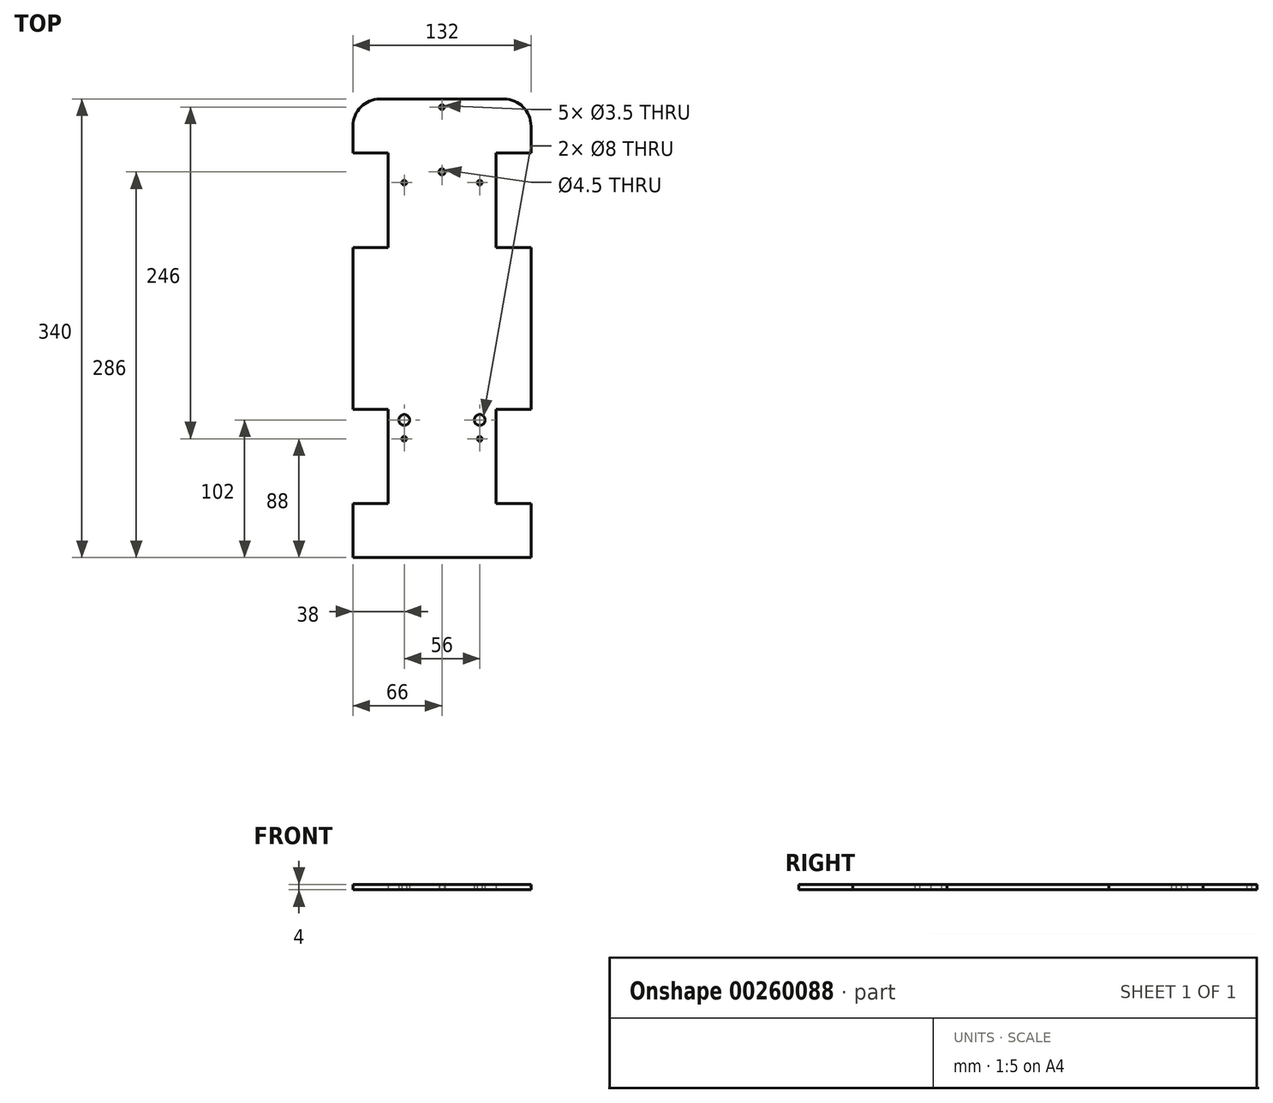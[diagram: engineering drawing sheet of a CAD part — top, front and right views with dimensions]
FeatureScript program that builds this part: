
annotation { "Feature Type Name" : "Feature", "Feature Type Description" : "" }
export const myFeature = defineFeature(function(context is Context, id is Id, definition is map)
    precondition{}
    {
        {
            var Q0;
            Q0=qCreatedBy(makeId("Top.planeOp"),FACE);
            var sketch = newSketch(context, id + "F0", { "sketchPlane" : qUnion([Q0])});
            skLineSegment(sketch, "E0.bottom", {"start": v(-66, 90) * mm, "end": v(0, 90) * mm});
            skLineSegment(sketch, "E0.top", {"start": v(-66, -230) * mm, "end": v(0, -230) * mm});
            skLineSegment(sketch, "E0.left", {"start": v(-66, 90) * mm, "end": v(-66, 70) * mm});
            skLineSegment(sketch, "E0.right", {"start": v(0, 90) * mm, "end": v(0, -230) * mm});
            skLineSegment(sketch, "E1.bottom", {"start": v(-66, 70) * mm, "end": v(-40, 70) * mm});
            skLineSegment(sketch, "E1.top", {"start": v(-66, 0) * mm, "end": v(-40, 0) * mm});
            skLineSegment(sketch, "E1.right", {"start": v(-40, 70) * mm, "end": v(-40, 0) * mm});
            skLineSegment(sketch, "E2.bottom", {"start": v(-66, -120) * mm, "end": v(-40, -120) * mm});
            skLineSegment(sketch, "E2.top", {"start": v(-66, -190) * mm, "end": v(-40, -190) * mm});
            skLineSegment(sketch, "E2.right", {"start": v(-40, -120) * mm, "end": v(-40, -190) * mm});
            skLineSegment(sketch, "E3.trimOffspring", {"start": v(-66, -190) * mm, "end": v(-66, -230) * mm});
            skLineSegment(sketch, "E4.trimOffspring", {"start": v(-66, 0) * mm, "end": v(-66, -120) * mm});
            skLineSegment(sketch, "E5.bottom", {"start": v(-46, 110) * mm, "end": v(-40, 110) * mm});
            skLineSegment(sketch, "E5.top", {"start": v(-66, 90) * mm, "end": v(-40, 90) * mm});
            skLineSegment(sketch, "E5.left", {"start": v(-66, 90) * mm, "end": v(-66, 90) * mm});
            skLineSegment(sketch, "E5.right", {"start": v(-40, 110) * mm, "end": v(-40, 90) * mm});
            skPoint(sketch, "E6.visualSharp", {"position": v(-66, 110) * mm});
            skArc(sketch, "E6.filletArc", {"start": v(-46, 110) * mm, "mid": v(-60.14, 104.14) * mm, "end": v(-66, 90) * mm});
            skLineSegment(sketch, "E7.bottom", {"start": v(-40, 110) * mm, "end": v(0, 110) * mm});
            skLineSegment(sketch, "E7.top", {"start": v(-40, 90) * mm, "end": v(0, 90) * mm});
            skLineSegment(sketch, "E7.right", {"start": v(0, 110) * mm, "end": v(0, 90) * mm});
            skLineSegment(sketch, "E8.MirrorCS", {"start": v(40, 110) * mm, "end": v(0, 110) * mm});
            skArc(sketch, "E9.MirrorCS", {"start": v(46, 110) * mm, "mid": v(60.14, 104.14) * mm, "end": v(66, 90) * mm});
            skLineSegment(sketch, "E10.MirrorCS", {"start": v(46, 110) * mm, "end": v(40, 110) * mm});
            skLineSegment(sketch, "E11.MirrorCS", {"start": v(66, 90) * mm, "end": v(0, 90) * mm});
            skLineSegment(sketch, "E12.MirrorCS", {"start": v(66, 90) * mm, "end": v(66, 70) * mm});
            skLineSegment(sketch, "E13.MirrorCS", {"start": v(66, 70) * mm, "end": v(40, 70) * mm});
            skLineSegment(sketch, "E14.MirrorCS", {"start": v(66, 0) * mm, "end": v(40, 0) * mm});
            skLineSegment(sketch, "E15.MirrorCS", {"start": v(40, 70) * mm, "end": v(40, 0) * mm});
            skLineSegment(sketch, "E16.MirrorCS", {"start": v(66, 0) * mm, "end": v(66, -120) * mm});
            skLineSegment(sketch, "E17.MirrorCS", {"start": v(40, -120) * mm, "end": v(40, -190) * mm});
            skLineSegment(sketch, "E18.MirrorCS", {"start": v(66, -120) * mm, "end": v(40, -120) * mm});
            skLineSegment(sketch, "E19.MirrorCS", {"start": v(66, -190) * mm, "end": v(40, -190) * mm});
            skLineSegment(sketch, "E20.MirrorCS", {"start": v(66, -190) * mm, "end": v(66, -230) * mm});
            skLineSegment(sketch, "E21.MirrorCS", {"start": v(66, -230) * mm, "end": v(0, -230) * mm});
            skLineSegment(sketch, "E22.left", {"start": v(-40, -120) * mm, "end": v(-40, -142) * mm});
            skLineSegment(sketch, "E23.right", {"start": v(-40, -142) * mm, "end": v(-40, -142) * mm});
            skLineSegment(sketch, "E24.MirrorCS", {"start": v(40, -142) * mm, "end": v(16, -142) * mm});
            skLineSegment(sketch, "E25.MirrorCS", {"start": v(28, -142) * mm, "end": v(40, -142) * mm});
            skLineSegment(sketch, "E26.top", {"start": v(-40, -128) * mm, "end": v(-28, -128) * mm});
            skLineSegment(sketch, "E26.left", {"start": v(-40, -120) * mm, "end": v(-40, -128) * mm});
            skLineSegment(sketch, "E26.right", {"start": v(-28, -120) * mm, "end": v(-28, -128) * mm});
            skLineSegment(sketch, "E27.MirrorCS", {"start": v(28, -120) * mm, "end": v(28, -128) * mm});
            skLineSegment(sketch, "E28.MirrorCS", {"start": v(40, -128) * mm, "end": v(28, -128) * mm});
            skLineSegment(sketch, "E29.bottom", {"start": v(-40, -142) * mm, "end": v(-28, -142) * mm});
            skLineSegment(sketch, "E29.left", {"start": v(-40, -142) * mm, "end": v(-40, -135.6) * mm});
            skLineSegment(sketch, "E29.right", {"start": v(-28, -142) * mm, "end": v(-28, -135.6) * mm});
            skLineSegment(sketch, "E30.top", {"start": v(-40, 48) * mm, "end": v(-28, 48) * mm});
            skLineSegment(sketch, "E30.left", {"start": v(-40, 70) * mm, "end": v(-40, 48) * mm});
            skLineSegment(sketch, "E30.right", {"start": v(-28, 52.96) * mm, "end": v(-28, 48) * mm});
            skLineSegment(sketch, "E31.bottom", {"start": v(-41.22, 70) * mm, "end": v(-40, 70) * mm});
            skLineSegment(sketch, "E32.MirrorCS", {"start": v(28, 52.96) * mm, "end": v(28, 48) * mm});
            skLineSegment(sketch, "E33.MirrorCS", {"start": v(40, 48) * mm, "end": v(28, 48) * mm});
            skLineSegment(sketch, "E34.left", {"start": v(-40, 62.87) * mm, "end": v(-40, 56) * mm});
            skLineSegment(sketch, "E34.right", {"start": v(0, 62.87) * mm, "end": v(0, 56) * mm});
            skLineSegment(sketch, "E35.bottom", {"start": v(-6.64, 110) * mm, "end": v(0, 110) * mm});
            skLineSegment(sketch, "E35.right", {"start": v(0, 110) * mm, "end": v(0, 104) * mm});
            skSolve(sketch);
        }
        {
            var Q0;
            Q0=makeQuery(id+"F0.imprint","IMPRINT",FACE,{"disambiguationData":[TD([[makeQuery(id+"F0.imprint","IMPRINT",EDGE,{"derivedFrom":sQuery(id+"F0.wireOp",EDGE,"E0.top")}),1.0]])]});
            var Q1;
            Q1=makeQuery(id+"F0.imprint","IMPRINT",FACE,{"disambiguationData":[TD([[makeQuery(id+"F0.imprint","IMPRINT",EDGE,{"derivedFrom":sQuery(id+"F0.wireOp",EDGE,"E0.right")}),1.0]])]});
            var Q2;
            Q2=makeQuery(id+"F0.imprint","IMPRINT",FACE,{"disambiguationData":[TD([[makeQuery(id+"F0.imprint","IMPRINT",EDGE,{"derivedFrom":sQuery(id+"F0.wireOp",EDGE,"E7.right")}),1.0]])]});
            var Q3;
            Q3=makeQuery(id+"F0.imprint","IMPRINT",FACE,{"disambiguationData":[TD([[makeQuery(id+"F0.imprint","IMPRINT",EDGE,{"derivedFrom":sQuery(id+"F0.wireOp",EDGE,"E7.bottom")}),-1.0]])]});
            var Q4;
            Q4=makeQuery(id+"F0.imprint","IMPRINT",FACE,{"disambiguationData":[TD([[makeQuery(id+"F0.imprint","IMPRINT",EDGE,{"derivedFrom":sQuery(id+"F0.wireOp",EDGE,"E5.bottom")}),-1.0]])]});
            extrude(context, id + "F1", {"entities" : qUnion([Q0, Q1, Q2, Q3, Q4]), "depth" : 4 * mm});
        }
        {
            var Q0;
            Q0=sQuery(id+"F0.wireOp",VERTEX,"E26.right.end");
            var Q1;
            Q1=makeQuery(id+"F1.opExtrude","SWEPT_BODY",BODY,{"disambiguationData":[OSD([sQuery(id+"F0.wireOp",EDGE,"E0.top"),sQuery(id+"F0.wireOp",EDGE,"E0.left"),sQuery(id+"F0.wireOp",EDGE,"E1.bottom"),sQuery(id+"F0.wireOp",EDGE,"E1.top"),sQuery(id+"F0.wireOp",EDGE,"E1.right"),sQuery(id+"F0.wireOp",EDGE,"E2.bottom"),sQuery(id+"F0.wireOp",EDGE,"E2.top"),sQuery(id+"F0.wireOp",EDGE,"E2.right"),sQuery(id+"F0.wireOp",EDGE,"E3.trimOffspring"),sQuery(id+"F0.wireOp",EDGE,"E4.trimOffspring"),sQuery(id+"F0.wireOp",EDGE,"E5.bottom"),sQuery(id+"F0.wireOp",EDGE,"E6.filletArc"),sQuery(id+"F0.wireOp",EDGE,"E7.bottom"),sQuery(id+"F0.wireOp",EDGE,"E8.MirrorCS"),sQuery(id+"F0.wireOp",EDGE,"E9.MirrorCS"),sQuery(id+"F0.wireOp",EDGE,"E10.MirrorCS"),sQuery(id+"F0.wireOp",EDGE,"E12.MirrorCS"),sQuery(id+"F0.wireOp",EDGE,"E13.MirrorCS"),sQuery(id+"F0.wireOp",EDGE,"E14.MirrorCS"),sQuery(id+"F0.wireOp",EDGE,"E15.MirrorCS"),sQuery(id+"F0.wireOp",EDGE,"E16.MirrorCS"),sQuery(id+"F0.wireOp",EDGE,"E17.MirrorCS"),sQuery(id+"F0.wireOp",EDGE,"E18.MirrorCS"),sQuery(id+"F0.wireOp",EDGE,"E19.MirrorCS"),sQuery(id+"F0.wireOp",EDGE,"E20.MirrorCS"),sQuery(id+"F0.wireOp",EDGE,"E21.MirrorCS"),sQuery(id+"F0.wireOp",EDGE,"E22.left"),sQuery(id+"F0.wireOp",EDGE,"E26.left")])]});
            hole(context, id + "F2", {"style" : HoleStyle.SIMPLE, "endStyle" : HoleEndStyle.THROUGH, "oppositeDirection" : true, "holeDiameter" : 8 * mm, "tappedDepth" : 12 * mm, "tapClearance" : 3, "locations" : qUnion([Q0]), "scope" : qUnion([Q1])});
        }
        {
            var Q0;
            Q0=sQuery(id+"F0.wireOp",VERTEX,"E29.bottom.end");
            var Q1;
            Q1=sQuery(id+"F0.wireOp",VERTEX,"E25.MirrorCS.start");
            var Q2;
            Q2=makeQuery(id+"F1.opExtrude","SWEPT_BODY",BODY,{"disambiguationData":[OSD([sQuery(id+"F0.wireOp",EDGE,"E0.top"),sQuery(id+"F0.wireOp",EDGE,"E0.left"),sQuery(id+"F0.wireOp",EDGE,"E1.bottom"),sQuery(id+"F0.wireOp",EDGE,"E1.top"),sQuery(id+"F0.wireOp",EDGE,"E1.right"),sQuery(id+"F0.wireOp",EDGE,"E2.bottom"),sQuery(id+"F0.wireOp",EDGE,"E2.top"),sQuery(id+"F0.wireOp",EDGE,"E2.right"),sQuery(id+"F0.wireOp",EDGE,"E3.trimOffspring"),sQuery(id+"F0.wireOp",EDGE,"E4.trimOffspring"),sQuery(id+"F0.wireOp",EDGE,"E5.bottom"),sQuery(id+"F0.wireOp",EDGE,"E6.filletArc"),sQuery(id+"F0.wireOp",EDGE,"E7.bottom"),sQuery(id+"F0.wireOp",EDGE,"E8.MirrorCS"),sQuery(id+"F0.wireOp",EDGE,"E9.MirrorCS"),sQuery(id+"F0.wireOp",EDGE,"E10.MirrorCS"),sQuery(id+"F0.wireOp",EDGE,"E12.MirrorCS"),sQuery(id+"F0.wireOp",EDGE,"E13.MirrorCS"),sQuery(id+"F0.wireOp",EDGE,"E14.MirrorCS"),sQuery(id+"F0.wireOp",EDGE,"E15.MirrorCS"),sQuery(id+"F0.wireOp",EDGE,"E16.MirrorCS"),sQuery(id+"F0.wireOp",EDGE,"E17.MirrorCS"),sQuery(id+"F0.wireOp",EDGE,"E18.MirrorCS"),sQuery(id+"F0.wireOp",EDGE,"E19.MirrorCS"),sQuery(id+"F0.wireOp",EDGE,"E20.MirrorCS"),sQuery(id+"F0.wireOp",EDGE,"E21.MirrorCS"),sQuery(id+"F0.wireOp",EDGE,"E22.left"),sQuery(id+"F0.wireOp",EDGE,"E26.left"),sQuery(id+"F0.wireOp",EDGE,"E29.left")])]});
            hole(context, id + "F3", {"style" : HoleStyle.SIMPLE, "endStyle" : HoleEndStyle.THROUGH, "oppositeDirection" : true, "holeDiameter" : 3.5 * mm, "tappedDepth" : 12 * mm, "tapClearance" : 3, "locations" : qUnion([Q0, Q1]), "scope" : qUnion([Q2])});
        }
        {
            var Q0;
            Q0=sQuery(id+"F0.wireOp",VERTEX,"E28.MirrorCS.end");
            var Q1;
            Q1=makeQuery(id+"F1.opExtrude","SWEPT_BODY",BODY,{"disambiguationData":[OSD([sQuery(id+"F0.wireOp",EDGE,"E0.top"),sQuery(id+"F0.wireOp",EDGE,"E0.left"),sQuery(id+"F0.wireOp",EDGE,"E1.bottom"),sQuery(id+"F0.wireOp",EDGE,"E1.top"),sQuery(id+"F0.wireOp",EDGE,"E1.right"),sQuery(id+"F0.wireOp",EDGE,"E2.bottom"),sQuery(id+"F0.wireOp",EDGE,"E2.top"),sQuery(id+"F0.wireOp",EDGE,"E2.right"),sQuery(id+"F0.wireOp",EDGE,"E3.trimOffspring"),sQuery(id+"F0.wireOp",EDGE,"E4.trimOffspring"),sQuery(id+"F0.wireOp",EDGE,"E5.bottom"),sQuery(id+"F0.wireOp",EDGE,"E6.filletArc"),sQuery(id+"F0.wireOp",EDGE,"E7.bottom"),sQuery(id+"F0.wireOp",EDGE,"E8.MirrorCS"),sQuery(id+"F0.wireOp",EDGE,"E9.MirrorCS"),sQuery(id+"F0.wireOp",EDGE,"E10.MirrorCS"),sQuery(id+"F0.wireOp",EDGE,"E12.MirrorCS"),sQuery(id+"F0.wireOp",EDGE,"E13.MirrorCS"),sQuery(id+"F0.wireOp",EDGE,"E14.MirrorCS"),sQuery(id+"F0.wireOp",EDGE,"E15.MirrorCS"),sQuery(id+"F0.wireOp",EDGE,"E16.MirrorCS"),sQuery(id+"F0.wireOp",EDGE,"E17.MirrorCS"),sQuery(id+"F0.wireOp",EDGE,"E18.MirrorCS"),sQuery(id+"F0.wireOp",EDGE,"E19.MirrorCS"),sQuery(id+"F0.wireOp",EDGE,"E20.MirrorCS"),sQuery(id+"F0.wireOp",EDGE,"E21.MirrorCS"),sQuery(id+"F0.wireOp",EDGE,"E22.left"),sQuery(id+"F0.wireOp",EDGE,"E26.left"),sQuery(id+"F0.wireOp",EDGE,"E29.left")])]});
            hole(context, id + "F4", {"style" : HoleStyle.SIMPLE, "endStyle" : HoleEndStyle.THROUGH, "oppositeDirection" : true, "holeDiameter" : 8 * mm, "tappedDepth" : 12 * mm, "tapClearance" : 3, "locations" : qUnion([Q0]), "scope" : qUnion([Q1])});
        }
        {
            var Q0;
            Q0=sQuery(id+"F0.wireOp",VERTEX,"E30.right.end");
            var Q1;
            Q1=sQuery(id+"F0.wireOp",VERTEX,"E32.MirrorCS.end");
            var Q2;
            Q2=makeQuery(id+"F1.opExtrude","SWEPT_BODY",BODY,{"disambiguationData":[OSD([sQuery(id+"F0.wireOp",EDGE,"E0.top"),sQuery(id+"F0.wireOp",EDGE,"E0.left"),sQuery(id+"F0.wireOp",EDGE,"E1.bottom"),sQuery(id+"F0.wireOp",EDGE,"E1.top"),sQuery(id+"F0.wireOp",EDGE,"E1.right"),sQuery(id+"F0.wireOp",EDGE,"E2.bottom"),sQuery(id+"F0.wireOp",EDGE,"E2.top"),sQuery(id+"F0.wireOp",EDGE,"E2.right"),sQuery(id+"F0.wireOp",EDGE,"E3.trimOffspring"),sQuery(id+"F0.wireOp",EDGE,"E4.trimOffspring"),sQuery(id+"F0.wireOp",EDGE,"E5.bottom"),sQuery(id+"F0.wireOp",EDGE,"E6.filletArc"),sQuery(id+"F0.wireOp",EDGE,"E7.bottom"),sQuery(id+"F0.wireOp",EDGE,"E8.MirrorCS"),sQuery(id+"F0.wireOp",EDGE,"E9.MirrorCS"),sQuery(id+"F0.wireOp",EDGE,"E10.MirrorCS"),sQuery(id+"F0.wireOp",EDGE,"E12.MirrorCS"),sQuery(id+"F0.wireOp",EDGE,"E13.MirrorCS"),sQuery(id+"F0.wireOp",EDGE,"E14.MirrorCS"),sQuery(id+"F0.wireOp",EDGE,"E15.MirrorCS"),sQuery(id+"F0.wireOp",EDGE,"E16.MirrorCS"),sQuery(id+"F0.wireOp",EDGE,"E17.MirrorCS"),sQuery(id+"F0.wireOp",EDGE,"E18.MirrorCS"),sQuery(id+"F0.wireOp",EDGE,"E19.MirrorCS"),sQuery(id+"F0.wireOp",EDGE,"E20.MirrorCS"),sQuery(id+"F0.wireOp",EDGE,"E21.MirrorCS"),sQuery(id+"F0.wireOp",EDGE,"E22.left"),sQuery(id+"F0.wireOp",EDGE,"E26.left"),sQuery(id+"F0.wireOp",EDGE,"E29.left"),sQuery(id+"F0.wireOp",EDGE,"E30.left"),sQuery(id+"F0.wireOp",EDGE,"E31.bottom")])]});
            hole(context, id + "F5", {"style" : HoleStyle.SIMPLE, "endStyle" : HoleEndStyle.THROUGH, "oppositeDirection" : true, "holeDiameter" : 3.5 * mm, "tappedDepth" : 12 * mm, "tapClearance" : 3, "locations" : qUnion([Q0, Q1]), "scope" : qUnion([Q2])});
        }
        {
            var Q0;
            Q0=sQuery(id+"F0.wireOp",VERTEX,"E34.right.end");
            var Q1;
            Q1=makeQuery(id+"F1.opExtrude","SWEPT_BODY",BODY,{"disambiguationData":[OSD([sQuery(id+"F0.wireOp",EDGE,"E0.top"),sQuery(id+"F0.wireOp",EDGE,"E0.left"),sQuery(id+"F0.wireOp",EDGE,"E1.bottom"),sQuery(id+"F0.wireOp",EDGE,"E1.top"),sQuery(id+"F0.wireOp",EDGE,"E1.right"),sQuery(id+"F0.wireOp",EDGE,"E2.bottom"),sQuery(id+"F0.wireOp",EDGE,"E2.top"),sQuery(id+"F0.wireOp",EDGE,"E2.right"),sQuery(id+"F0.wireOp",EDGE,"E3.trimOffspring"),sQuery(id+"F0.wireOp",EDGE,"E4.trimOffspring"),sQuery(id+"F0.wireOp",EDGE,"E5.bottom"),sQuery(id+"F0.wireOp",EDGE,"E6.filletArc"),sQuery(id+"F0.wireOp",EDGE,"E7.bottom"),sQuery(id+"F0.wireOp",EDGE,"E8.MirrorCS"),sQuery(id+"F0.wireOp",EDGE,"E9.MirrorCS"),sQuery(id+"F0.wireOp",EDGE,"E10.MirrorCS"),sQuery(id+"F0.wireOp",EDGE,"E12.MirrorCS"),sQuery(id+"F0.wireOp",EDGE,"E13.MirrorCS"),sQuery(id+"F0.wireOp",EDGE,"E14.MirrorCS"),sQuery(id+"F0.wireOp",EDGE,"E15.MirrorCS"),sQuery(id+"F0.wireOp",EDGE,"E16.MirrorCS"),sQuery(id+"F0.wireOp",EDGE,"E17.MirrorCS"),sQuery(id+"F0.wireOp",EDGE,"E18.MirrorCS"),sQuery(id+"F0.wireOp",EDGE,"E19.MirrorCS"),sQuery(id+"F0.wireOp",EDGE,"E20.MirrorCS"),sQuery(id+"F0.wireOp",EDGE,"E21.MirrorCS"),sQuery(id+"F0.wireOp",EDGE,"E22.left"),sQuery(id+"F0.wireOp",EDGE,"E26.left"),sQuery(id+"F0.wireOp",EDGE,"E29.left"),sQuery(id+"F0.wireOp",EDGE,"E30.left"),sQuery(id+"F0.wireOp",EDGE,"E31.bottom"),sQuery(id+"F0.wireOp",EDGE,"E34.left")])]});
            hole(context, id + "F6", {"style" : HoleStyle.SIMPLE, "endStyle" : HoleEndStyle.THROUGH, "oppositeDirection" : true, "holeDiameter" : 4.5 * mm, "tappedDepth" : 12 * mm, "tapClearance" : 3, "locations" : qUnion([Q0]), "scope" : qUnion([Q1])});
        }
        {
            var Q0;
            Q0=sQuery(id+"F0.wireOp",VERTEX,"E35.right.end");
            var Q1;
            Q1=makeQuery(id+"F1.opExtrude","SWEPT_BODY",BODY,{"disambiguationData":[OSD([sQuery(id+"F0.wireOp",EDGE,"E0.top"),sQuery(id+"F0.wireOp",EDGE,"E0.left"),sQuery(id+"F0.wireOp",EDGE,"E1.bottom"),sQuery(id+"F0.wireOp",EDGE,"E1.top"),sQuery(id+"F0.wireOp",EDGE,"E1.right"),sQuery(id+"F0.wireOp",EDGE,"E2.bottom"),sQuery(id+"F0.wireOp",EDGE,"E2.top"),sQuery(id+"F0.wireOp",EDGE,"E2.right"),sQuery(id+"F0.wireOp",EDGE,"E3.trimOffspring"),sQuery(id+"F0.wireOp",EDGE,"E4.trimOffspring"),sQuery(id+"F0.wireOp",EDGE,"E5.bottom"),sQuery(id+"F0.wireOp",EDGE,"E6.filletArc"),sQuery(id+"F0.wireOp",EDGE,"E7.bottom"),sQuery(id+"F0.wireOp",EDGE,"E8.MirrorCS"),sQuery(id+"F0.wireOp",EDGE,"E9.MirrorCS"),sQuery(id+"F0.wireOp",EDGE,"E10.MirrorCS"),sQuery(id+"F0.wireOp",EDGE,"E12.MirrorCS"),sQuery(id+"F0.wireOp",EDGE,"E13.MirrorCS"),sQuery(id+"F0.wireOp",EDGE,"E14.MirrorCS"),sQuery(id+"F0.wireOp",EDGE,"E15.MirrorCS"),sQuery(id+"F0.wireOp",EDGE,"E16.MirrorCS"),sQuery(id+"F0.wireOp",EDGE,"E17.MirrorCS"),sQuery(id+"F0.wireOp",EDGE,"E18.MirrorCS"),sQuery(id+"F0.wireOp",EDGE,"E19.MirrorCS"),sQuery(id+"F0.wireOp",EDGE,"E20.MirrorCS"),sQuery(id+"F0.wireOp",EDGE,"E21.MirrorCS"),sQuery(id+"F0.wireOp",EDGE,"E22.left"),sQuery(id+"F0.wireOp",EDGE,"E26.left"),sQuery(id+"F0.wireOp",EDGE,"E29.left"),sQuery(id+"F0.wireOp",EDGE,"E30.left"),sQuery(id+"F0.wireOp",EDGE,"E31.bottom"),sQuery(id+"F0.wireOp",EDGE,"E34.left"),sQuery(id+"F0.wireOp",EDGE,"E35.bottom")])]});
            hole(context, id + "F7", {"style" : HoleStyle.SIMPLE, "endStyle" : HoleEndStyle.THROUGH, "oppositeDirection" : true, "holeDiameter" : 3.5 * mm, "tappedDepth" : 12 * mm, "tapClearance" : 3, "locations" : qUnion([Q0]), "scope" : qUnion([Q1])});
        }
    });
